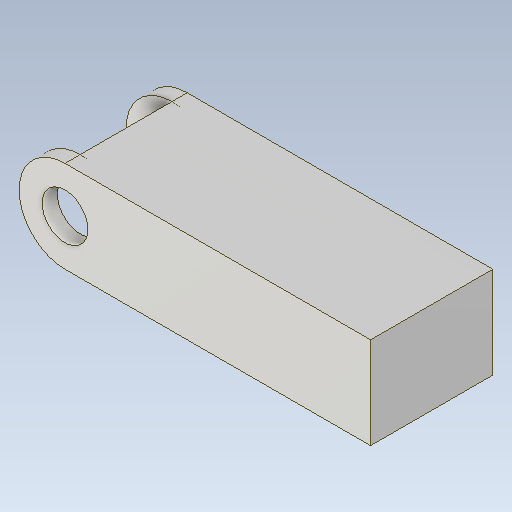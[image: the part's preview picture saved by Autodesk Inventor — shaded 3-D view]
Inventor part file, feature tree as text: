
AUTODESK INVENTOR PART (.ipt)
format: ipt  version: 2021.4 (Build 254397000, 397)  size: 101,376 bytes
history: imported  units: in
note: dims shown in document units (in); Inventor stores cm internally (conversion verified against a paired STEP export)
features: imported_body x1
ambient origin geometry x8: Origin, YZ Plane, XZ Plane, XY Plane, X Axis, Y Axis, Z Axis, Center Point
bodies: Solid1 (imported_parasolid), Body1 (imported_parasolid)
feature tree (1):
  imported_body  NMx_Import_Brep_tag  [imported B-rep: ~12 faces, bbox_mm=[1000.0, 300.0, 400.0]]
